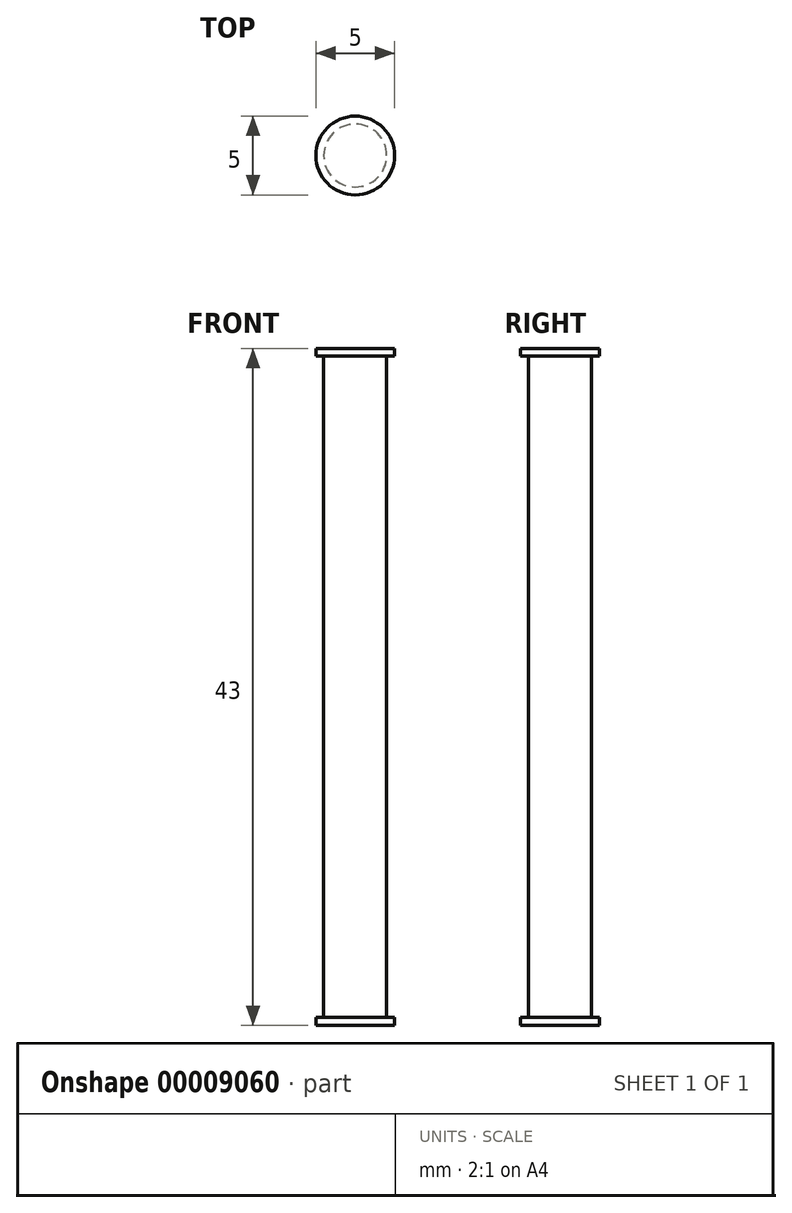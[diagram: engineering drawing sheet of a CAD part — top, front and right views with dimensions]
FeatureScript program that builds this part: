
annotation { "Feature Type Name" : "Feature", "Feature Type Description" : "" }
export const myFeature = defineFeature(function(context is Context, id is Id, definition is map)
    precondition{}
    {
        {
            var Q0;
            Q0=qCreatedBy(makeId("Top.planeOp"),FACE);
            var sketch = newSketch(context, id + "F0", { "sketchPlane" : qUnion([Q0])});
            skCircle(sketch, "E0", {"center": v(0, 0) * mm, "radius": 2 * mm});
            skSolve(sketch);
        }
        {
            var Q0;
            Q0 = qSketchRegion(id + "F0", true);
            extrude(context, id + "F1", {"entities" : qUnion([Q0]), "depth" : 42 * mm});
        }
        {
            var Q0;
            Q0=makeQuery(id+"F1.opExtrude","CAP_FACE",FACE,{"disambiguationData":[OSD([sQuery(id+"F0.wireOp",EDGE,"E0")])],"isStart":false});
            var sketch = newSketch(context, id + "F2", { "sketchPlane" : qUnion([Q0])});
            skCircle(sketch, "E1", {"center": v(0, 0) * mm, "radius": 2.5 * mm});
            skSolve(sketch);
        }
        {
            var Q0;
            Q0 = qSketchRegion(id + "F2", true);
            extrude(context, id + "F3", {"entities" : qUnion([Q0]), "operationType" : NewBodyOperationType.ADD, "depth" : 0.5 * mm});
        }
        {
            var Q0;
            Q0=makeQuery(id+"F1.opExtrude","CAP_FACE",FACE,{"disambiguationData":[OSD([sQuery(id+"F0.wireOp",EDGE,"E0")])],"isStart":true});
            var sketch = newSketch(context, id + "F4", { "sketchPlane" : qUnion([Q0])});
            skCircle(sketch, "E2", {"center": v(0, 0) * mm, "radius": 2.5 * mm});
            skSolve(sketch);
        }
        {
            var Q0;
            Q0 = qSketchRegion(id + "F4", true);
            extrude(context, id + "F5", {"entities" : qUnion([Q0]), "operationType" : NewBodyOperationType.ADD, "depth" : 0.5 * mm});
        }
    });
